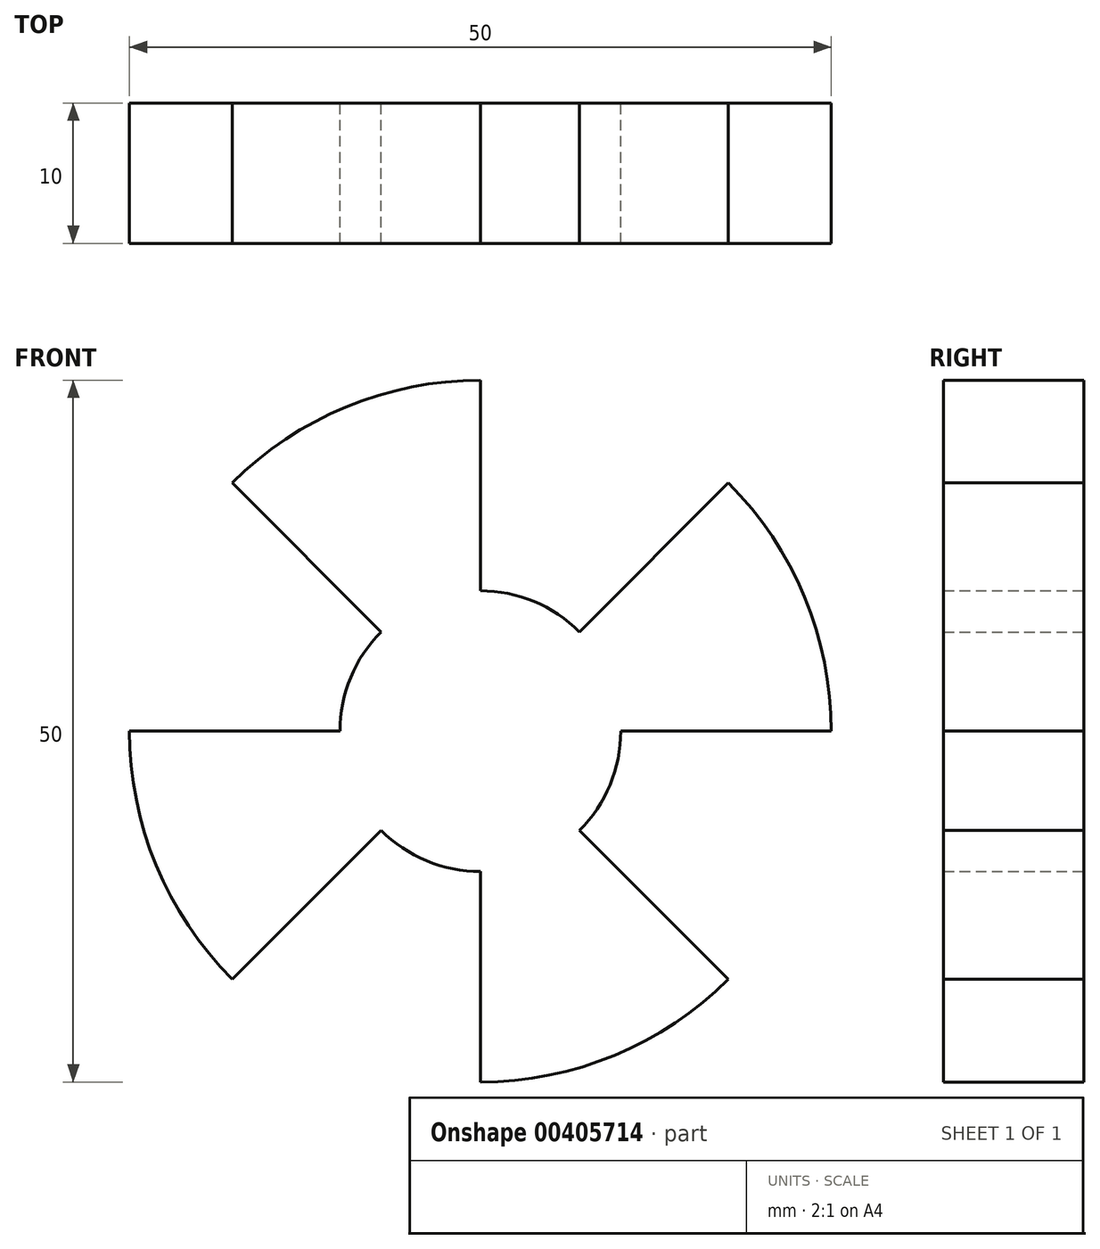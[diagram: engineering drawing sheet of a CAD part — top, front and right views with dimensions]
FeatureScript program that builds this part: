
annotation { "Feature Type Name" : "Feature", "Feature Type Description" : "" }
export const myFeature = defineFeature(function(context is Context, id is Id, definition is map)
    precondition{}
    {
        {
            var Q0;
            Q0=qCreatedBy(makeId("Front.planeOp"),FACE);
            var sketch = newSketch(context, id + "F0", { "sketchPlane" : qUnion([Q0])});
            skArc(sketch, "E0", {"start": v(-25, 0) * mm, "mid": v(-23.1, -9.57) * mm, "end": v(-17.68, -17.68) * mm});
            skArc(sketch, "E1", {"start": v(-7.07, 7.07) * mm, "mid": v(-9.24, 3.83) * mm, "end": v(-10, 0) * mm});
            skLineSegment(sketch, "E2", {"start": v(0, 10) * mm, "end": v(0, 25) * mm});
            skLineSegment(sketch, "E3", {"start": v(0, -10) * mm, "end": v(0, -25) * mm});
            skLineSegment(sketch, "E4", {"start": v(-10, 0) * mm, "end": v(-25, 0) * mm});
            skLineSegment(sketch, "E5", {"start": v(10, 0) * mm, "end": v(25, 0) * mm});
            skLineSegment(sketch, "E6", {"start": v(7.07, 7.07) * mm, "end": v(17.68, 17.68) * mm});
            skLineSegment(sketch, "E7", {"start": v(-7.07, -7.07) * mm, "end": v(-17.68, -17.68) * mm});
            skLineSegment(sketch, "E8", {"start": v(-7.07, 7.07) * mm, "end": v(-17.68, 17.68) * mm});
            skLineSegment(sketch, "E9", {"start": v(7.07, -7.07) * mm, "end": v(17.68, -17.68) * mm});
            skArc(sketch, "E10.trimOffspring", {"start": v(0, -25) * mm, "mid": v(9.57, -23.1) * mm, "end": v(17.68, -17.68) * mm});
            skArc(sketch, "E11.trimOffspring", {"start": v(25, 0) * mm, "mid": v(23.1, 9.57) * mm, "end": v(17.68, 17.68) * mm});
            skArc(sketch, "E12.trimOffspring", {"start": v(0, 25) * mm, "mid": v(-9.57, 23.1) * mm, "end": v(-17.68, 17.68) * mm});
            skArc(sketch, "E13.trimOffspring", {"start": v(-7.07, -7.07) * mm, "mid": v(-3.83, -9.24) * mm, "end": v(0, -10) * mm});
            skArc(sketch, "E14.trimOffspring", {"start": v(7.07, -7.07) * mm, "mid": v(9.24, -3.83) * mm, "end": v(10, 0) * mm});
            skArc(sketch, "E15.trimOffspring", {"start": v(7.07, 7.07) * mm, "mid": v(3.83, 9.24) * mm, "end": v(0, 10) * mm});
            skSolve(sketch);
        }
        {
            var Q0;
            Q0=makeQuery(id+"F0.imprint","IMPRINT",FACE,{"disambiguationData":[TD([[makeQuery(id+"F0.imprint","IMPRINT",EDGE,{"derivedFrom":sQuery(id+"F0.wireOp",EDGE,"E0")}),1.0]])]});
            extrude(context, id + "F1", {"entities" : qUnion([Q0]), "depth" : 10 * mm});
        }
    });
